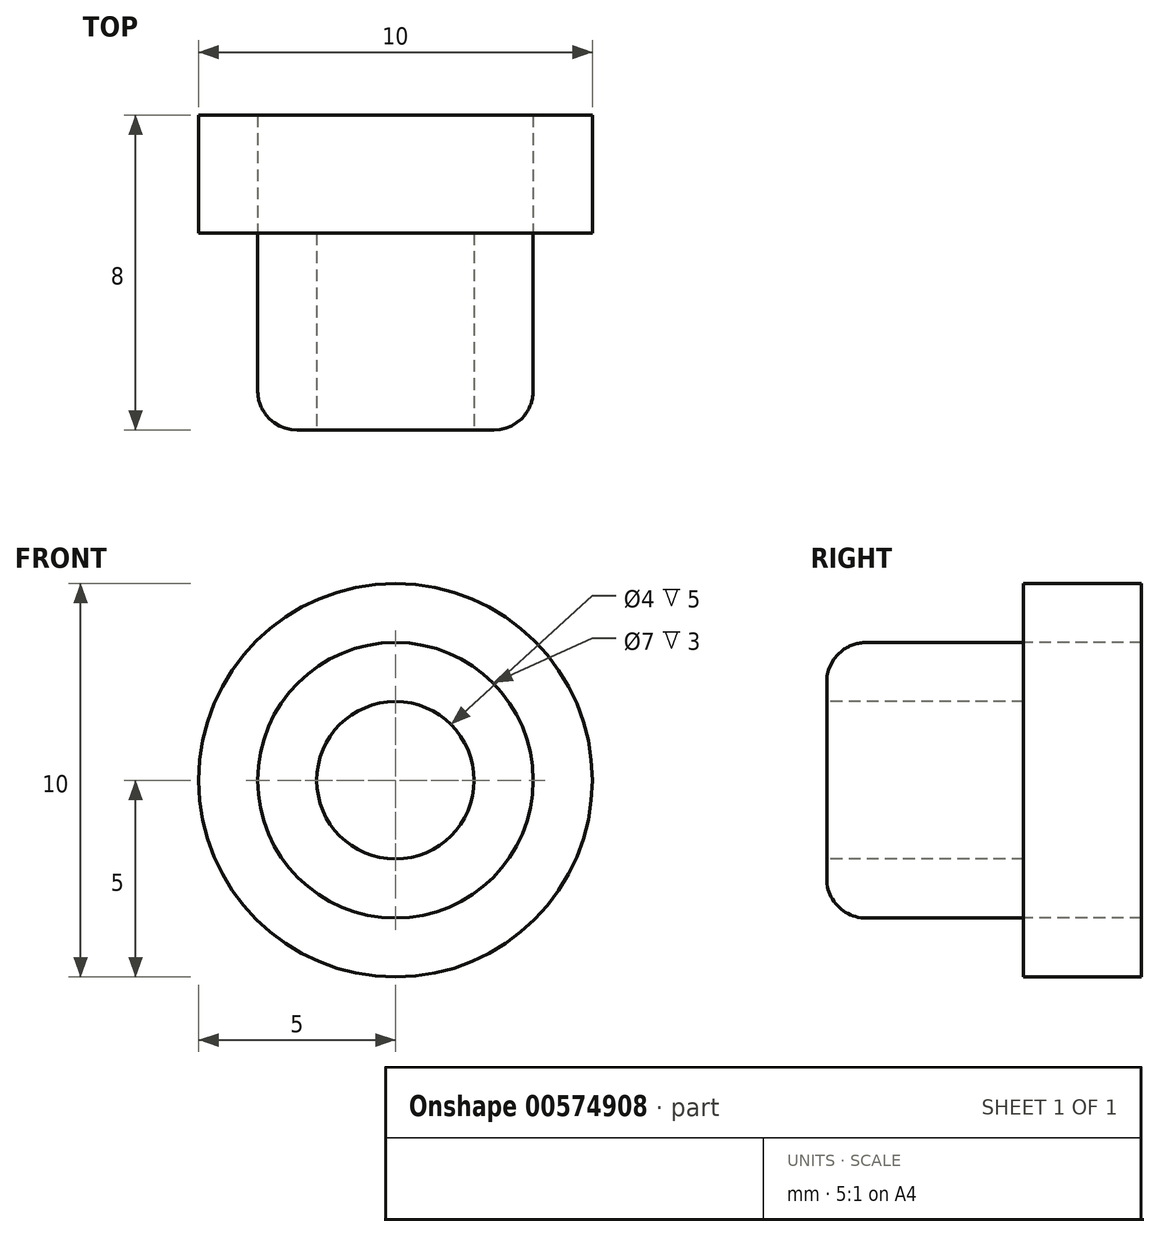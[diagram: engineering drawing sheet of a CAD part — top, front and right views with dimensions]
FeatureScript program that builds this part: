
annotation { "Feature Type Name" : "Feature", "Feature Type Description" : "" }
export const myFeature = defineFeature(function(context is Context, id is Id, definition is map)
    precondition{}
    {
        {
            var Q0;
            Q0=qCreatedBy(makeId("Front.planeOp"),FACE);
            var sketch = newSketch(context, id + "F0", { "sketchPlane" : qUnion([Q0])});
            skCircle(sketch, "E0", {"center": v(0, 0) * mm, "radius": 5 * mm});
            skCircle(sketch, "E1", {"center": v(0, 0) * mm, "radius": 3.5 * mm});
            skSolve(sketch);
        }
        {
            var Q0;
            Q0=makeQuery(id+"F0.imprint","IMPRINT",FACE,{"disambiguationData":[TD([[makeQuery(id+"F0.imprint","IMPRINT",EDGE,{"derivedFrom":sQuery(id+"F0.wireOp",EDGE,"E0")}),1.0]])]});
            extrude(context, id + "F1", {"entities" : qUnion([Q0]), "oppositeDirection" : true, "depth" : 3 * mm, "offsetDistance" : 25 * mm});
        }
        {
            var Q0;
            Q0=makeQuery(id+"F0.imprint","IMPRINT",FACE,{"disambiguationData":[TD([[makeQuery(id+"F0.imprint","IMPRINT",EDGE,{"derivedFrom":sQuery(id+"F0.wireOp",EDGE,"E1")}),1.0]])]});
            extrude(context, id + "F2", {"entities" : qUnion([Q0]), "depth" : 5 * mm, "offsetDistance" : 25 * mm});
        }
        {
            var Q0;
            Q0=makeQuery(id+"F2.opExtrude","CAP_FACE",FACE,{"disambiguationData":[OSD([sQuery(id+"F0.wireOp",EDGE,"E1")])],"isStart":false});
            var sketch = newSketch(context, id + "F3", { "sketchPlane" : qUnion([Q0])});
            skCircle(sketch, "E2", {"center": v(0, 0) * mm, "radius": 2 * mm});
            skSolve(sketch);
        }
        {
            var Q0;
            Q0=makeQuery(id+"F3.imprint","IMPRINT",FACE,{"disambiguationData":[TD([[makeQuery(id+"F3.imprint","IMPRINT",EDGE,{"derivedFrom":sQuery(id+"F3.wireOp",EDGE,"E2")}),1.0]])]});
            extrude(context, id + "F4", {"entities" : qUnion([Q0]), "operationType" : NewBodyOperationType.REMOVE, "oppositeDirection" : true, "depth" : 5 * mm, "offsetDistance" : 25 * mm});
        }
        {
            var Q0;
            Q0=makeQuery(id+"F2.opExtrude","CAP_EDGE",EDGE,{"disambiguationData":[OSD([sQuery(id+"F0.wireOp",EDGE,"E1")])],"isStart":false});
            fillet(context, id + "F5", {"entities" : qUnion([Q0]), "radius" : 1 * mm, "tangentPropagation" : true, "allowEdgeOverflow" : false});
        }
    });
